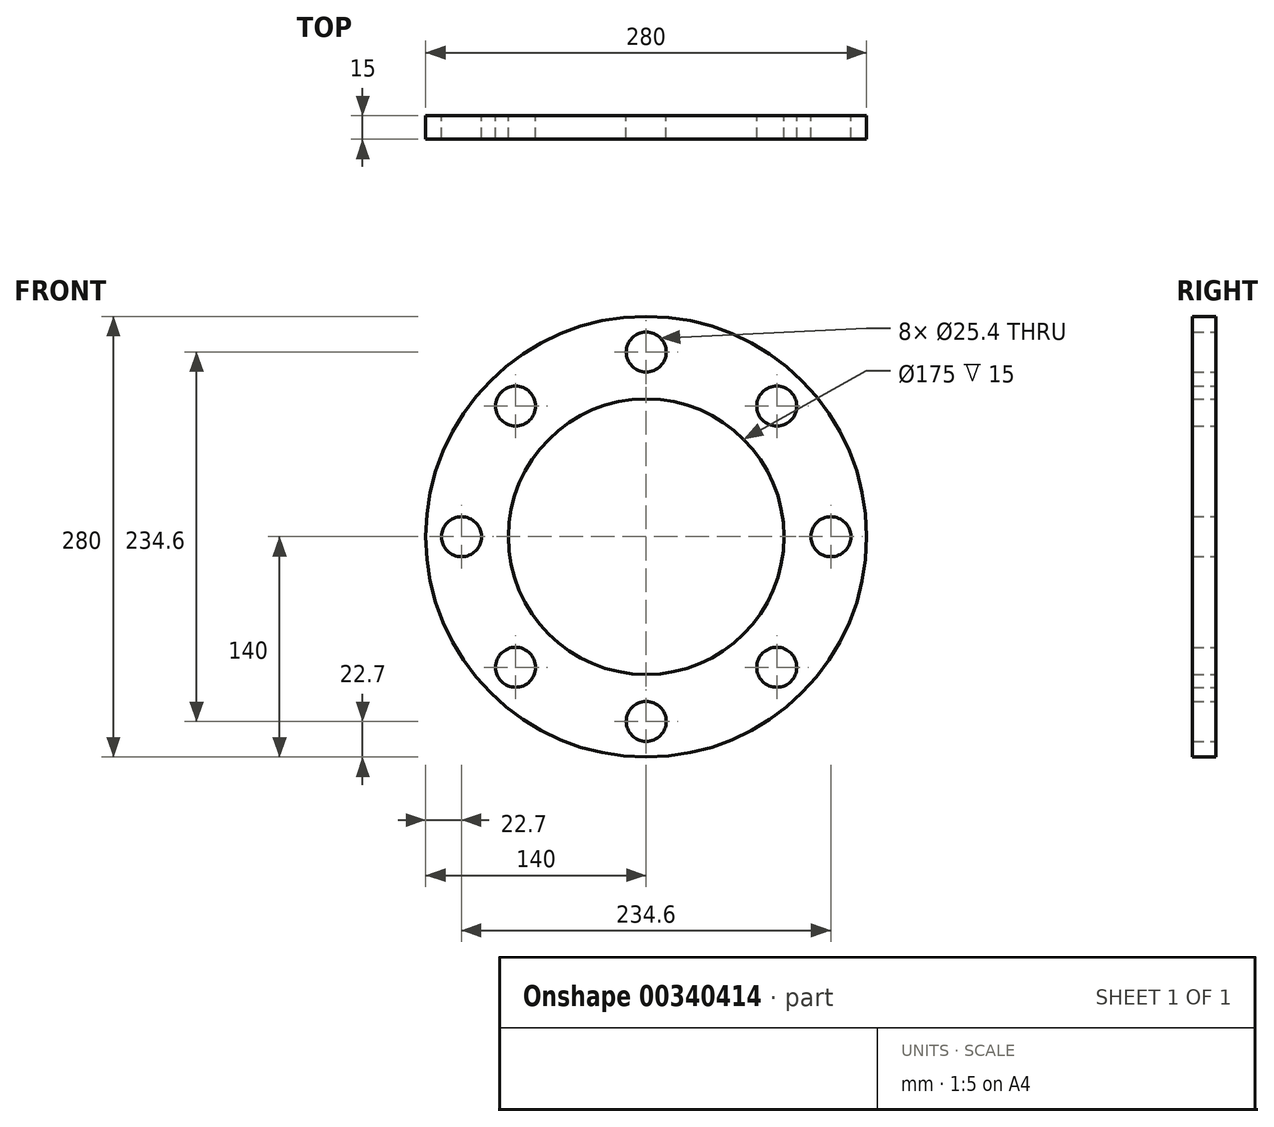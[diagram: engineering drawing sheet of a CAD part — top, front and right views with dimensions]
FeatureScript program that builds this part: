
annotation { "Feature Type Name" : "Feature", "Feature Type Description" : "" }
export const myFeature = defineFeature(function(context is Context, id is Id, definition is map)
    precondition{}
    {
        {
            var Q0;
            Q0=qCreatedBy(makeId("Front.planeOp"),FACE);
            var sketch = newSketch(context, id + "F0", { "sketchPlane" : qUnion([Q0])});
            skCircle(sketch, "E0", {"center": v(0, 0) * mm, "radius": 140 * mm});
            skCircle(sketch, "E1", {"center": v(0, 117.3) * mm, "radius": 12.7 * mm});
            skCircle(sketch, "E2.1.0", {"center": v(-82.94, 82.94) * mm, "radius": 12.7 * mm});
            skCircle(sketch, "E2.2.0", {"center": v(-117.3, 0) * mm, "radius": 12.7 * mm});
            skCircle(sketch, "E3.1.3.0", {"center": v(-82.94, -82.94) * mm, "radius": 12.7 * mm});
            skCircle(sketch, "E3.1.4.0", {"center": v(0, -117.3) * mm, "radius": 12.7 * mm});
            skCircle(sketch, "E3.1.5.0", {"center": v(82.94, -82.94) * mm, "radius": 12.7 * mm});
            skCircle(sketch, "E3.1.6.0", {"center": v(117.3, 0) * mm, "radius": 12.7 * mm});
            skCircle(sketch, "E3.1.7.0", {"center": v(82.94, 82.94) * mm, "radius": 12.7 * mm});
            skCircle(sketch, "E4", {"center": v(0, 0) * mm, "radius": 87.5 * mm});
            skSolve(sketch);
        }
        {
            var Q0;
            Q0 = qSketchRegion(id + "F0", true);
            extrude(context, id + "F1", {"entities" : qUnion([Q0]), "depth" : 15 * mm});
        }
    });
